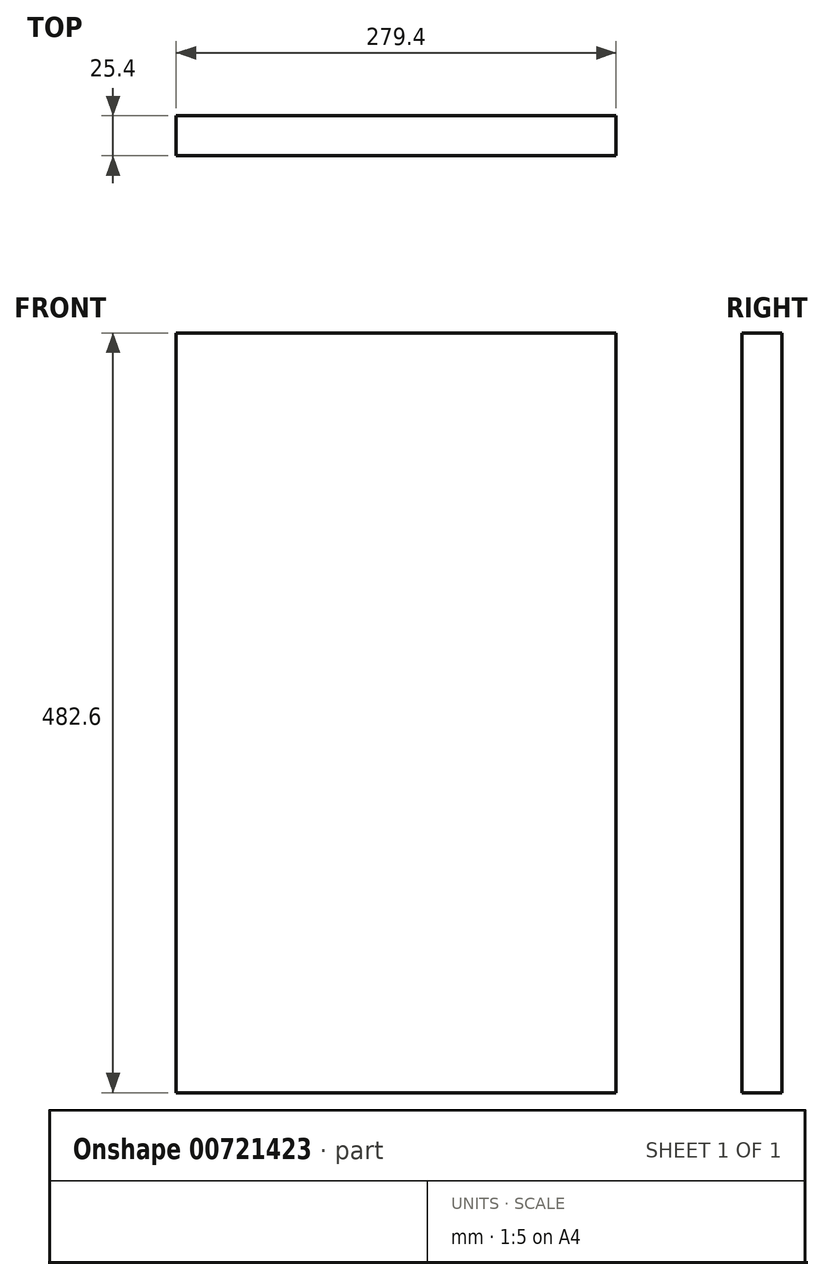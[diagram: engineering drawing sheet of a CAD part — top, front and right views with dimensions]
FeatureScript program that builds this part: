
annotation { "Feature Type Name" : "Feature", "Feature Type Description" : "" }
export const myFeature = defineFeature(function(context is Context, id is Id, definition is map)
    precondition{}
    {
        {
            var Q0;
            Q0=qCreatedBy(makeId("Front.planeOp"),FACE);
            var sketch = newSketch(context, id + "F0", { "sketchPlane" : qUnion([Q0])});
            skLineSegment(sketch, "E0.bottom", {"start": v(-133.86, 358.63) * mm, "end": v(145.54, 358.63) * mm});
            skLineSegment(sketch, "E0.top", {"start": v(-133.86, -123.97) * mm, "end": v(145.54, -123.97) * mm});
            skLineSegment(sketch, "E0.left", {"start": v(-133.86, 358.63) * mm, "end": v(-133.86, -123.97) * mm});
            skLineSegment(sketch, "E0.right", {"start": v(145.54, 358.63) * mm, "end": v(145.54, -123.97) * mm});
            skSolve(sketch);
        }
        {
            var Q0;
            Q0 = qSketchRegion(id + "F0", true);
            extrude(context, id + "F1", {"entities" : qUnion([Q0]), "depth" : 25.4 * mm, "offsetDistance" : 25.4 * mm});
        }
    });
